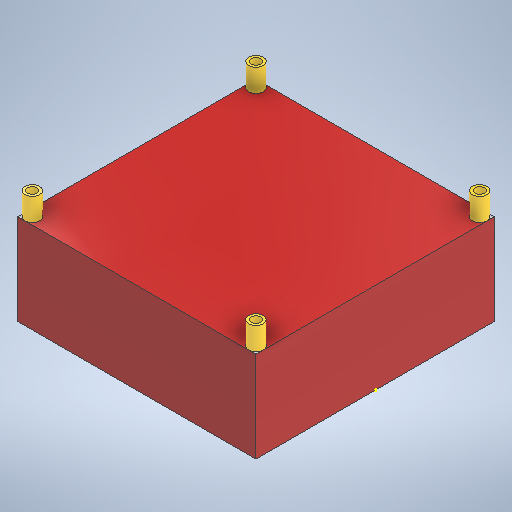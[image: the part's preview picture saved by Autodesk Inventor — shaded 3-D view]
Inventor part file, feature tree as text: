
AUTODESK INVENTOR PART (.ipt)
format: ipt  version: 2025.1 (Build 291241020, 241B)  size: 242,688 bytes
history: native  units: in
note: dims shown in document units (in); Inventor stores cm internally (conversion verified against a paired STEP export)
features: sketch x4, extrude x3
ambient origin geometry x8: Origin, YZ Plane, XZ Plane, XY Plane, X Axis, Y Axis, Z Axis, Center Point
bodies: Solid1 (feature_tree)
feature tree (7):
  extrude  "Extrusion1"  Depth=0.56in TaperAngle=0.0deg
  sketch  "Sketch2"  dims[d3=0.09in d4=0.09in]
  extrude  "Extrusion2"  Depth=0.09in
  extrude  "Extrusion3"  Depth=0.09in
  sketch  "Sketch1"  dims[d0=1.47in d1=0.56in d2=0.0in]
  sketch  "Sketch3"  dims[d5=0.09in d6=0.09in]
  sketch  "Sketch4"  dims[d7=0.14in d8=0.0in d9=0.0591in d10=0.0591in d11=0.0591in d12=0.0591in d13=0.14in d14=0.0in]
